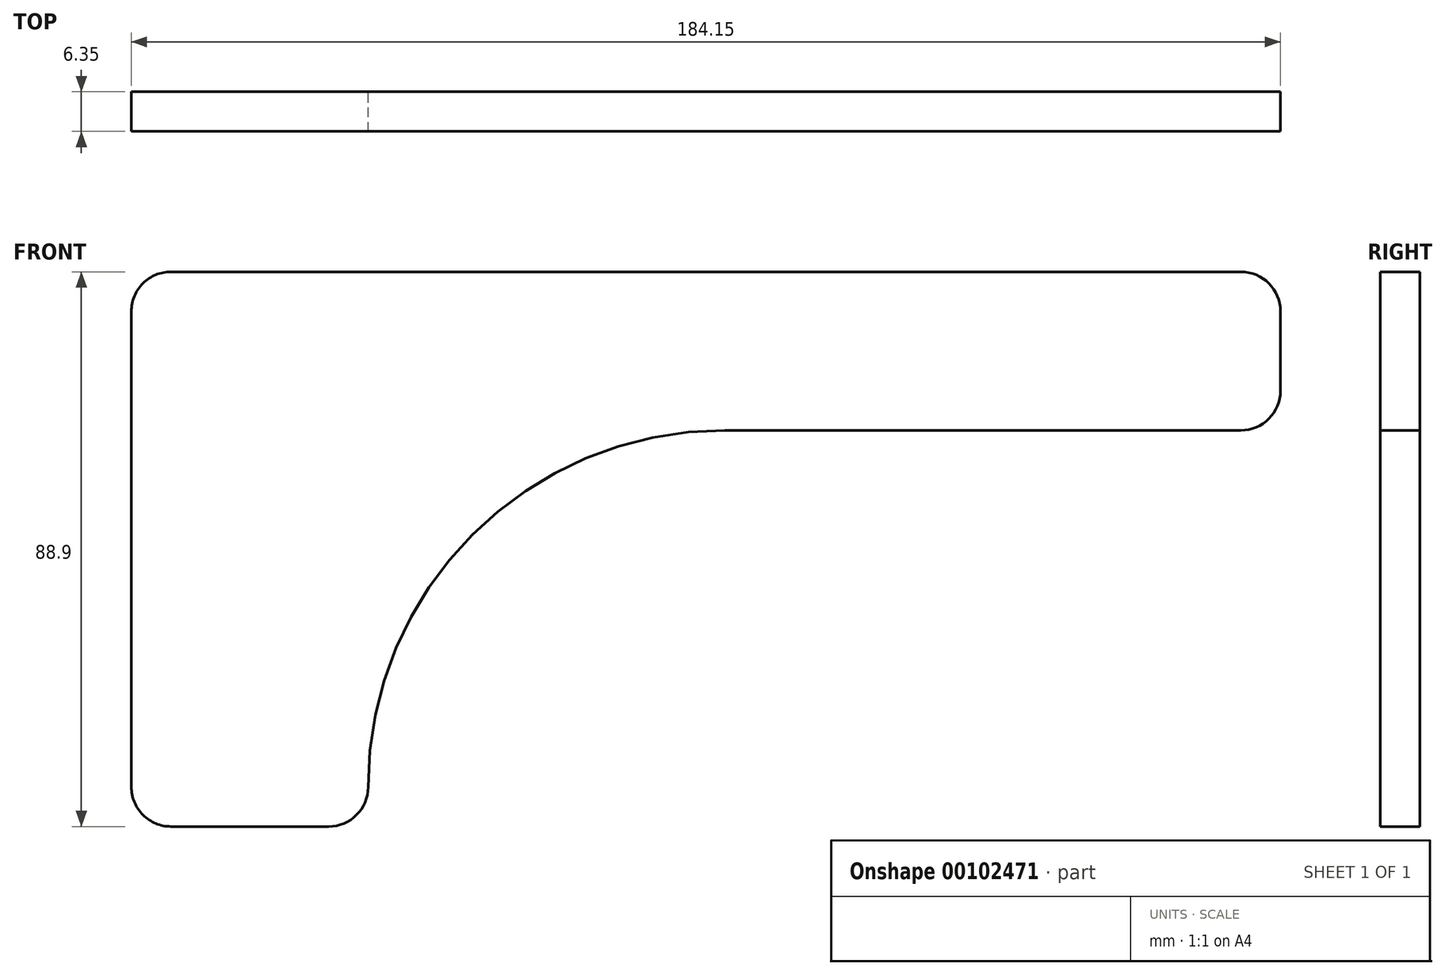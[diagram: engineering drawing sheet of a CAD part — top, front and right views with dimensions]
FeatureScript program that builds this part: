
annotation { "Feature Type Name" : "Feature", "Feature Type Description" : "" }
export const myFeature = defineFeature(function(context is Context, id is Id, definition is map)
    precondition{}
    {
        {
            var Q0;
            Q0=qCreatedBy(makeId("Front.planeOp"),FACE);
            var sketch = newSketch(context, id + "F0", { "sketchPlane" : qUnion([Q0])});
            skLineSegment(sketch, "E0", {"start": v(92.07, 38.1) * mm, "end": v(92.07, 25.4) * mm});
            skLineSegment(sketch, "E1", {"start": v(85.72, 44.45) * mm, "end": v(-85.73, 44.45) * mm});
            skLineSegment(sketch, "E2", {"start": v(-92.08, 38.1) * mm, "end": v(-92.07, -38.1) * mm});
            skArc(sketch, "E3", {"start": v(3.02, 19.05) * mm, "mid": v(-37.39, 2.31) * mm, "end": v(-54.13, -38.1) * mm});
            skLineSegment(sketch, "E4", {"start": v(3.02, 19.05) * mm, "end": v(85.72, 19.05) * mm});
            skLineSegment(sketch, "E5", {"start": v(-60.48, -44.45) * mm, "end": v(-85.72, -44.45) * mm});
            skArc(sketch, "E6", {"start": v(92.07, 38.1) * mm, "mid": v(90.22, 42.6) * mm, "end": v(85.72, 44.45) * mm});
            skArc(sketch, "E7", {"start": v(-85.73, 44.45) * mm, "mid": v(-90.22, 42.6) * mm, "end": v(-92.07, 38.1) * mm});
            skArc(sketch, "E8", {"start": v(-92.07, -38.1) * mm, "mid": v(-90.21, -42.6) * mm, "end": v(-85.72, -44.45) * mm});
            skArc(sketch, "E9", {"start": v(-60.48, -44.45) * mm, "mid": v(-55.99, -42.6) * mm, "end": v(-54.13, -38.1) * mm});
            skArc(sketch, "E10", {"start": v(85.72, 19.05) * mm, "mid": v(90.22, 20.9) * mm, "end": v(92.07, 25.4) * mm});
            skSolve(sketch);
        }
        {
            var Q0;
            Q0 = qSketchRegion(id + "F0", true);
            var Q1;
            Q1 = qConstructionFilter(qBodyType(qCreatedBy(id + "F0" ,EDGE), BodyType.WIRE), ConstructionObject.NO);
            extrude(context, id + "F1", {"entities" : qUnion([Q0]), "surfaceEntities" : qUnion([Q1]), "depth" : 6.35 * mm});
        }
    });
